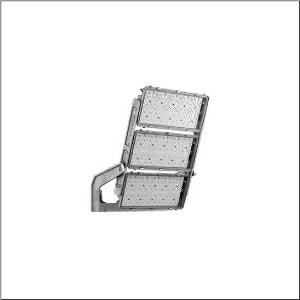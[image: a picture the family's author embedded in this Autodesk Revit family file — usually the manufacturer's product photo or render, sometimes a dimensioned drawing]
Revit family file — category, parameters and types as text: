
# Revit family: floodlight_fl_11_maxi_pro_remote___pl52_5xa779426d01ba_5366
name_source: partatom
category: Lighting Fixtures
units: mm (PartAtom-declared; Revit-internal decimal feet)

## family parameters
Cut with Voids When Loaded = No
Host = Face
Light Source = No
Part Type = Normal
Room Calculation Point = No
Round Connector Dimension = Use Diameter
Shared = No

## types (1)
- --- (1 x LED, 146220 lm, 1095.8 W, 4000K)
    Apparent Load = 1096 VA
    CIE Flux Codes = 24 55 98 100 100
    Color Rendering = 70
    Color Temperature = 4000K
    Default Elevation = 1800 mm
    Description = Floodlight FL 11  maxi  pro Remote floodlight; light control with lens of PMMA; cover panel of toughened safety glass, transparent; light distribution: PL52, asymmetric direct distribution, LEDcolour temperature: 4000K, rated luminous flux: 146.220lm, colour rendering: CRI > 70, light colour: 740; luminous efficacy: 133lm/W; brightness control: DALI 2 (1 DALI address); with terminal, 8-pole, max. 2.5mm², mains connection: 220..240V/380..400V AC, 50/60Hz, surge voltage resistance: line to ground: 10kV, ECG replaceable separately, LED unit replaceable without ESD environment, dustproof LED module, dimming range 10..100%, no afterglow with DALI off / DMX off command; 1096W floodlight with 3x LED unit of diecast aluminium, coated grey; length: 713mm / width: 651mm / height: 338mm; mounting bracket, of diecast aluminium, uncoated, natural, equipment: Longlife, protection rating (complete): IP66; insulation class (complete): insulation class I (protective earthing); certification: CE, ENEC, VDE; ball protection: ball impact resistance with accessories, impact resistance: IK07; rated ambient temperature 10°C, only for outdoor installations, permissible operating ambient temperature: -40..+40°C, permissible storage temperature: -40..+85°Cpackaging unit: 1 piece

Light Distribution: PL52
    Height = 320 mm
    Lamp = 1 x LED
    Lamp Light Flux = 146220 lm
    Lamp Power = 1095.8 W
    Lamp count = 1
    Length = 1002 mm
    Luminous efficacy = 133 lm/W
    Manufacturer = Siteco
    ModVariant = No
    Model = 5XA779426D01BA
    Mounting Place = Ceiling
    Mounting Type = Surface mounted
    Number of Poles = 1
    OnlyDefault = Yes
    Power Factor = 1
    Product Name = Floodlight FL 11 maxi pro Remote | PL52
    Product group = floodlight | ceiling mounted
    ProductGroupID = 301
    Protection Class = Protection class I
    Protection Degree = IP 66
    RLX_Detail_Level = 1
    RLX_Emergency_Light_Flux = 0 lm
    RLX_Emergency_Type = 0
    RLX_Emergency_Type_DB = No
    RlxData = <blob elided: 52277 chars, md5=b94e0162>
    Socket = socket
    Standby Power = 0 W
    System Light Flux = 146220 lm
    System Power = 1096 W
    Type Comments = factory setting: luminous flux: 100 % | dim-lin: 254 | 760 mA
    Type Image = l_1349141.jpg
    URL = http://relux.com
    VarID = @adj_097860
    Voltage = 0 V
    Weight = 0.00 kg
    Width = 655 mm

## geometry (parser evidence)
native form markers: Blend x4, Sweep x14
no freeform markers — native parametric forms only
